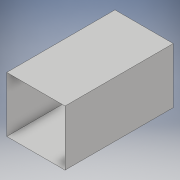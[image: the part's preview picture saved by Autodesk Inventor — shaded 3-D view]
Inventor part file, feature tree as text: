
AUTODESK INVENTOR PART (.ipt)
format: ipt  version: 2017 (Build 210142000, 142)  size: 89,088 bytes
history: native  units: in
note: dims shown in document units (in); Inventor stores cm internally (conversion verified against a paired STEP export)
features: extrude x1, other x1, sketch x1
ambient origin geometry x8: Origin, YZ Plane, XZ Plane, XY Plane, X Axis, Y Axis, Z Axis, Center Point
bodies: Solid1 (feature_tree)
feature tree (3):
  extrude  "Extrusion1"  Depth=7.0in
  other  "enterences"
  sketch  "Sketch1"  dims[d0=6.6667in d1=7.0in d2=13.0in d3=0.0in]
